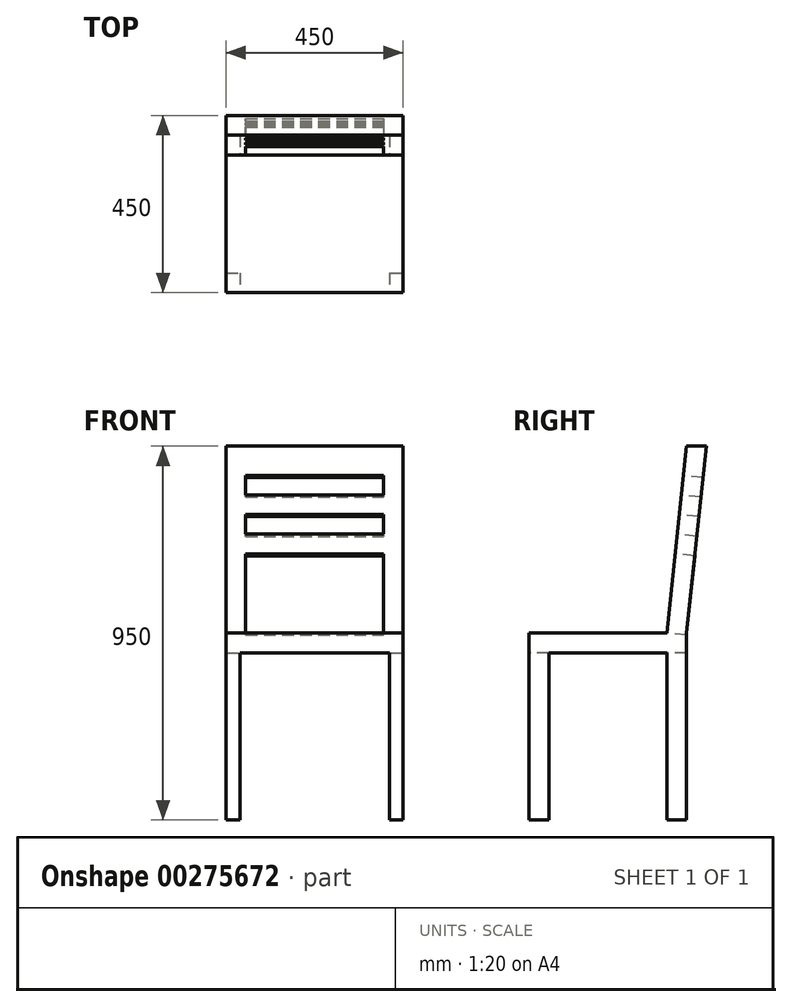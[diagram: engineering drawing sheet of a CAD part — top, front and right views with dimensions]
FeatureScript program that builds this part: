
annotation { "Feature Type Name" : "Feature", "Feature Type Description" : "" }
export const myFeature = defineFeature(function(context is Context, id is Id, definition is map)
    precondition{}
    {
        {
            var Q0;
            Q0=qCreatedBy(makeId("Top.planeOp"),FACE);
            var sketch = newSketch(context, id + "F0", { "sketchPlane" : qUnion([Q0])});
            skLineSegment(sketch, "E0.bottom", {"start": v(225, 225) * mm, "end": v(-225, 225) * mm});
            skLineSegment(sketch, "E0.top", {"start": v(225, -225) * mm, "end": v(-225, -225) * mm});
            skLineSegment(sketch, "E0.left", {"start": v(225, 225) * mm, "end": v(225, -225) * mm});
            skLineSegment(sketch, "E0.right", {"start": v(-225, 225) * mm, "end": v(-225, -225) * mm});
            skPoint(sketch, "E0.middle", {"position": v(0, 0) * mm});
            skSolve(sketch);
        }
        {
            var Q0;
            Q0=qSketchRegion(id+"F0",true);
            extrude(context, id + "F1", {"entities" : qUnion([Q0]), "depth" : 950 * mm});
        }
        {
            var Q0;
            Q0=makeQuery(id+"F1.opExtrude","SWEPT_FACE",FACE,{"disambiguationData":[OSD([sQuery(id+"F0.wireOp",EDGE,"E0.left")])]});
            var sketch = newSketch(context, id + "F2", { "sketchPlane" : qUnion([Q0])});
            skLineSegment(sketch, "E1.bottom", {"start": v(225, 475) * mm, "end": v(-225, 475) * mm});
            skLineSegment(sketch, "E1.top", {"start": v(225, 425) * mm, "end": v(-225, 425) * mm});
            skLineSegment(sketch, "E1.left", {"start": v(225, 475) * mm, "end": v(225, 425) * mm});
            skLineSegment(sketch, "E1.right", {"start": v(-225, 475) * mm, "end": v(-225, 425) * mm});
            skLineSegment(sketch, "E2", {"start": v(-175, 0) * mm, "end": v(-175, 425) * mm});
            skLineSegment(sketch, "E3", {"start": v(175, 0) * mm, "end": v(175, 425) * mm});
            skLineSegment(sketch, "E4", {"start": v(125, 0) * mm, "end": v(125, 425) * mm});
            skLineSegment(sketch, "E5", {"start": v(225, 950) * mm, "end": v(175, 475) * mm});
            skLineSegment(sketch, "E6", {"start": v(125, 475) * mm, "end": v(175, 950) * mm});
            skLineSegment(sketch, "E7", {"start": v(175, 475) * mm, "end": v(175, 425) * mm});
            skSolve(sketch);
        }
        {
            var Q0;
            {var subQ4=sQuery(id+"F2.wireOp",EDGE,"E6");Q0=makeQuery(id+"F2.imprint","IMPRINT",FACE,{"disambiguationData":[TD([[makeQuery(id+"F2.imprint","IMPRINT",EDGE,{"derivedFrom":subQ4}),1.0]])]});}
            var Q1;
            {var subQ4=sQuery(id+"F2.wireOp",EDGE,"E5");Q1=makeQuery(id+"F2.imprint","IMPRINT",FACE,{"disambiguationData":[TD([[makeQuery(id+"F2.imprint","IMPRINT",EDGE,{"derivedFrom":subQ4}),1.0]])]});}
            var Q2;
            {var subQ0=sQuery(id+"F2.wireOp",EDGE,"E1.left");Q2=makeQuery(id+"F2.imprint","IMPRINT",FACE,{"disambiguationData":[TD([[makeQuery(id+"F2.imprint","IMPRINT",EDGE,{"derivedFrom":subQ0}),-1.0]])]});}
            var Q3;
            {var subQ4=sQuery(id+"F2.wireOp",EDGE,"E3");Q3=makeQuery(id+"F2.imprint","IMPRINT",FACE,{"disambiguationData":[TD([[makeQuery(id+"F2.imprint","IMPRINT",EDGE,{"derivedFrom":subQ4}),-1.0]])]});}
            var Q4;
            {var subQ0=sQuery(id+"F2.wireOp",EDGE,"E2");Q4=makeQuery(id+"F2.imprint","IMPRINT",FACE,{"disambiguationData":[TD([[makeQuery(id+"F2.imprint","IMPRINT",EDGE,{"derivedFrom":subQ0}),-1.0]])]});}
            extrude(context, id + "F3", {"entities" : qUnion([Q0, Q1, Q2, Q3, Q4]), "operationType" : NewBodyOperationType.REMOVE, "endBound" : BoundingType.THROUGH_ALL, "oppositeDirection" : true, "depth" : 25 * mm});
        }
        {
            var Q0;
            Q0=makeQuery(id+"F1.opExtrude","SWEPT_FACE",FACE,{"disambiguationData":[OSD([sQuery(id+"F0.wireOp",EDGE,"E0.top")])]});
            var sketch = newSketch(context, id + "F4", { "sketchPlane" : qUnion([Q0])});
            skLineSegment(sketch, "E8", {"start": v(-190, 0) * mm, "end": v(-190, 425) * mm});
            skLineSegment(sketch, "E9", {"start": v(-190, 425) * mm, "end": v(190, 425) * mm});
            skLineSegment(sketch, "E10", {"start": v(190, 425) * mm, "end": v(190, 0) * mm});
            skSolve(sketch);
        }
        {
            var Q0;
            {var subQ0=sQuery(id+"F4.wireOp",EDGE,"E8");Q0=makeQuery(id+"F4.imprint","IMPRINT",FACE,{"disambiguationData":[TD([[makeQuery(id+"F4.imprint","IMPRINT",EDGE,{"derivedFrom":subQ0}),-1.0]])]});}
            extrude(context, id + "F5", {"entities" : qUnion([Q0]), "operationType" : NewBodyOperationType.REMOVE, "endBound" : BoundingType.THROUGH_ALL, "oppositeDirection" : true, "depth" : 25 * mm});
        }
        {
            var Q0;
            Q0=makeQuery(id+"F3.boolean.opBoolean","COPY",FACE,{"derivedFrom":makeQuery(id+"F3.opExtrude","SWEPT_FACE",FACE,{"disambiguationData":[OSD([sQuery(id+"F2.wireOp",EDGE,"E6")])]})});
            var sketch = newSketch(context, id + "F6", { "sketchPlane" : qUnion([Q0])});
            skLineSegment(sketch, "E11", {"start": v(-175, 485.48) * mm, "end": v(-175, 888.1) * mm});
            skLineSegment(sketch, "E12", {"start": v(-175, 888.1) * mm, "end": v(175, 888.1) * mm});
            skLineSegment(sketch, "E13", {"start": v(175, 888.1) * mm, "end": v(175, 485.48) * mm});
            skLineSegment(sketch, "E14", {"start": v(-175, 838.1) * mm, "end": v(175, 838.1) * mm});
            skLineSegment(sketch, "E15", {"start": v(-175, 788.1) * mm, "end": v(175, 788.1) * mm});
            skLineSegment(sketch, "E16", {"start": v(-175, 738.1) * mm, "end": v(175, 738.1) * mm});
            skLineSegment(sketch, "E17", {"start": v(-175, 688.1) * mm, "end": v(175, 688.1) * mm});
            skSolve(sketch);
        }
        {
            var Q0;
            {var subQ3=sQuery(id+"F6.wireOp",EDGE,"E17");Q0=makeQuery(id+"F6.imprint","IMPRINT",FACE,{"disambiguationData":[TD([[makeQuery(id+"F6.imprint","IMPRINT",EDGE,{"derivedFrom":subQ3}),-1.0]])]});}
            var Q1;
            {var subQ0=sQuery(id+"F6.wireOp",EDGE,"E15");Q1=makeQuery(id+"F6.imprint","IMPRINT",FACE,{"disambiguationData":[TD([[makeQuery(id+"F6.imprint","IMPRINT",EDGE,{"derivedFrom":subQ0}),-1.0]])]});}
            var Q2;
            {var subQ0=sQuery(id+"F6.wireOp",EDGE,"E12");Q2=makeQuery(id+"F6.imprint","IMPRINT",FACE,{"disambiguationData":[TD([[makeQuery(id+"F6.imprint","IMPRINT",EDGE,{"derivedFrom":subQ0}),-1.0]])]});}
            extrude(context, id + "F7", {"entities" : qUnion([Q0, Q1, Q2]), "operationType" : NewBodyOperationType.REMOVE, "endBound" : BoundingType.THROUGH_ALL, "oppositeDirection" : true, "depth" : 25 * mm});
        }
    });
